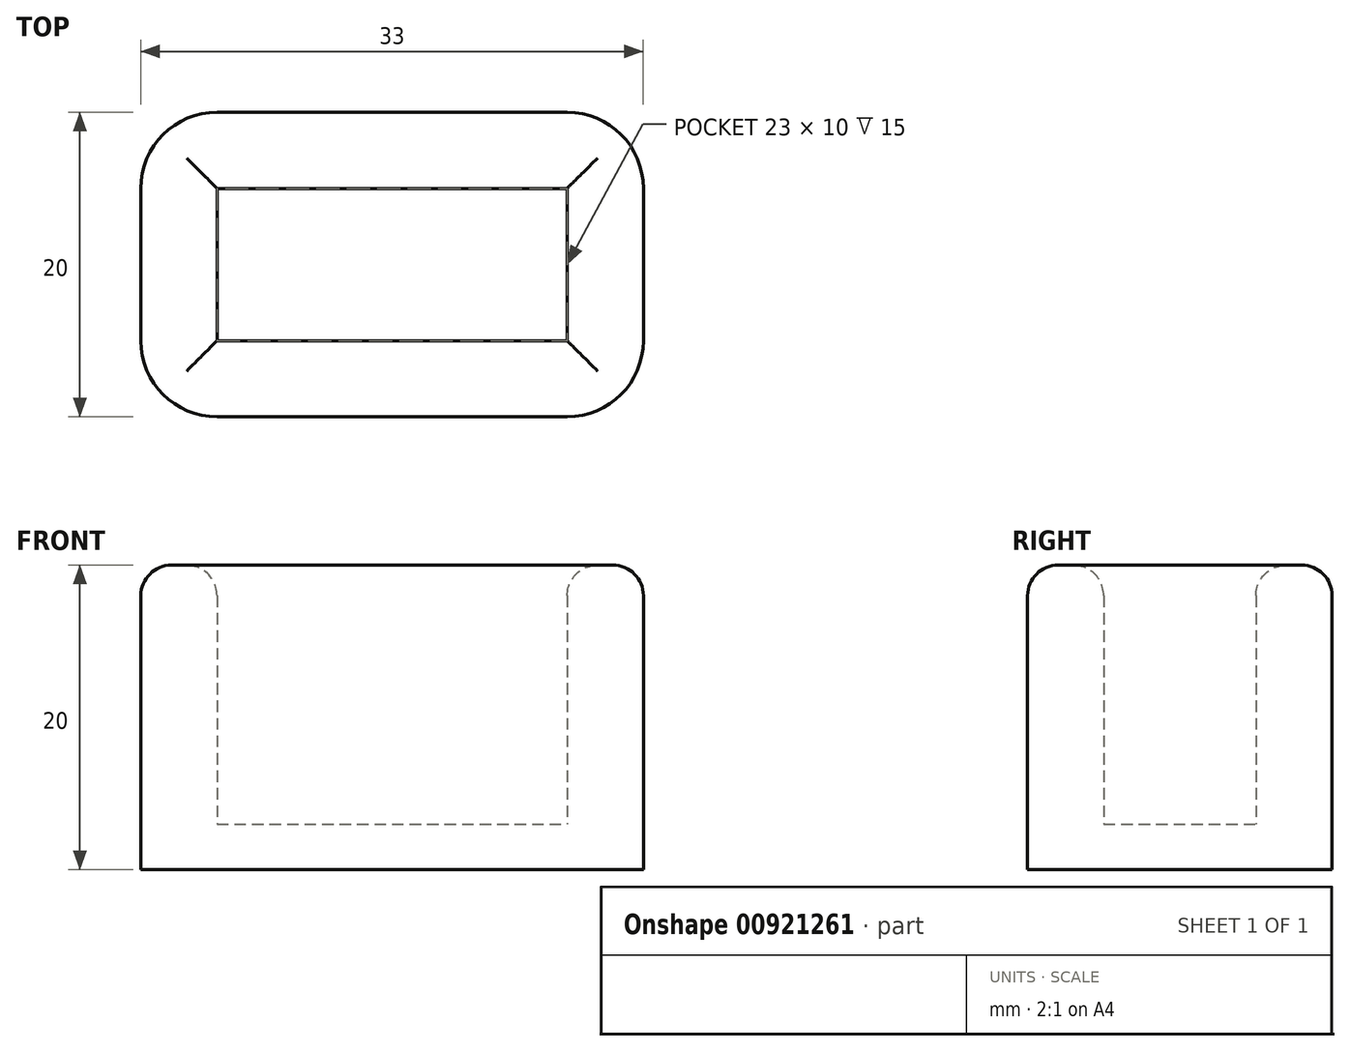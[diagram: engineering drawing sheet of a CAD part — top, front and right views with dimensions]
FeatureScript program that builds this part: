
annotation { "Feature Type Name" : "Feature", "Feature Type Description" : "" }
export const myFeature = defineFeature(function(context is Context, id is Id, definition is map)
    precondition{}
    {
        {
            var Q0;
            Q0=qCreatedBy(makeId("Top.planeOp"),FACE);
            var sketch = newSketch(context, id + "F0", { "sketchPlane" : qUnion([Q0])});
            skLineSegment(sketch, "E0.bottom", {"start": v(-38.39, 0) * mm, "end": v(-15.39, 0) * mm});
            skLineSegment(sketch, "E0.top", {"start": v(-38.39, 10) * mm, "end": v(-15.39, 10) * mm});
            skLineSegment(sketch, "E0.left", {"start": v(-38.39, 0) * mm, "end": v(-38.39, 10) * mm});
            skLineSegment(sketch, "E0.right", {"start": v(-15.39, 0) * mm, "end": v(-15.39, 10) * mm});
            skLineSegment(sketch, "E1.bottom", {"start": v(-38.39, 10) * mm, "end": v(-38.39, 10) * mm});
            skLineSegment(sketch, "E1.top", {"start": v(-38.39, 0) * mm, "end": v(-38.39, 0) * mm});
            skLineSegment(sketch, "E1.left", {"start": v(-38.39, 10) * mm, "end": v(-38.39, 0) * mm});
            skLineSegment(sketch, "E1.right", {"start": v(-38.39, 10) * mm, "end": v(-38.39, 0) * mm});
            skLineSegment(sketch, "E2.bottom", {"start": v(-15.39, 0) * mm, "end": v(-10.39, 0) * mm, "construction": true});
            skLineSegment(sketch, "E2.top", {"start": v(-15.39, 10) * mm, "end": v(-10.39, 10) * mm, "construction": true});
            skLineSegment(sketch, "E2.left", {"start": v(-15.39, 0) * mm, "end": v(-15.39, 10) * mm, "construction": true});
            skLineSegment(sketch, "E2.right", {"start": v(-10.39, 0) * mm, "end": v(-10.39, 10) * mm, "construction": true});
            skLineSegment(sketch, "E3.bottom", {"start": v(-38.39, 0) * mm, "end": v(-43.39, 0) * mm, "construction": true});
            skLineSegment(sketch, "E3.top", {"start": v(-38.39, 10) * mm, "end": v(-43.39, 10) * mm, "construction": true});
            skLineSegment(sketch, "E3.left", {"start": v(-38.39, 0) * mm, "end": v(-38.39, 10) * mm, "construction": true});
            skLineSegment(sketch, "E3.right", {"start": v(-43.39, 0) * mm, "end": v(-43.39, 10) * mm, "construction": true});
            skLineSegment(sketch, "E4.bottom", {"start": v(-38.39, 10) * mm, "end": v(-15.39, 10) * mm, "construction": true});
            skLineSegment(sketch, "E4.top", {"start": v(-38.39, 15) * mm, "end": v(-15.39, 15) * mm, "construction": true});
            skLineSegment(sketch, "E4.left", {"start": v(-38.39, 10) * mm, "end": v(-38.39, 15) * mm, "construction": true});
            skLineSegment(sketch, "E4.right", {"start": v(-15.39, 10) * mm, "end": v(-15.39, 15) * mm, "construction": true});
            skLineSegment(sketch, "E5.bottom", {"start": v(-15.39, 0) * mm, "end": v(-38.39, 0) * mm, "construction": true});
            skLineSegment(sketch, "E5.top", {"start": v(-15.39, -5) * mm, "end": v(-38.39, -5) * mm, "construction": true});
            skLineSegment(sketch, "E5.left", {"start": v(-15.39, 0) * mm, "end": v(-15.39, -5) * mm, "construction": true});
            skLineSegment(sketch, "E5.right", {"start": v(-38.39, 0) * mm, "end": v(-38.39, -5) * mm, "construction": true});
            skLineSegment(sketch, "E6.top", {"start": v(-38.39, 15) * mm, "end": v(-43.39, 15) * mm, "construction": true});
            skLineSegment(sketch, "E6.right", {"start": v(-43.39, 10) * mm, "end": v(-43.39, 15) * mm, "construction": true});
            skLineSegment(sketch, "E7.top", {"start": v(-38.39, -5) * mm, "end": v(-43.39, -5) * mm, "construction": true});
            skLineSegment(sketch, "E7.right", {"start": v(-43.39, 0) * mm, "end": v(-43.39, -5) * mm, "construction": true});
            skLineSegment(sketch, "E8.top", {"start": v(-15.39, -5) * mm, "end": v(-10.39, -5) * mm, "construction": true});
            skLineSegment(sketch, "E8.right", {"start": v(-10.39, 0) * mm, "end": v(-10.39, -5) * mm, "construction": true});
            skLineSegment(sketch, "E9.top", {"start": v(-15.39, 15) * mm, "end": v(-10.39, 15) * mm, "construction": true});
            skLineSegment(sketch, "E9.right", {"start": v(-10.39, 10) * mm, "end": v(-10.39, 15) * mm, "construction": true});
            skLineSegment(sketch, "E10.bottom", {"start": v(-43.39, 15) * mm, "end": v(-10.39, 15) * mm});
            skLineSegment(sketch, "E10.top", {"start": v(-43.39, -5) * mm, "end": v(-10.39, -5) * mm});
            skLineSegment(sketch, "E10.left", {"start": v(-43.39, 15) * mm, "end": v(-43.39, -5) * mm});
            skLineSegment(sketch, "E10.right", {"start": v(-10.39, 15) * mm, "end": v(-10.39, -5) * mm});
            skSolve(sketch);
        }
        {
            var Q0;
            Q0=makeQuery(id+"F0.imprint","IMPRINT",FACE,{"disambiguationData":[TD([[makeQuery(id+"F0.imprint","IMPRINT",EDGE,{"derivedFrom":sQuery(id+"F0.wireOp",EDGE,"E0.bottom")}),-1.0]])]});
            extrude(context, id + "F1", {"entities" : qUnion([Q0]), "depth" : 20 * mm, "offsetDistance" : 25 * mm});
        }
        {
            var Q0;
            Q0=makeQuery(id+"F0.imprint","IMPRINT",FACE,{"disambiguationData":[TD([[makeQuery(id+"F0.imprint","IMPRINT",EDGE,{"derivedFrom":sQuery(id+"F0.wireOp",EDGE,"E0.bottom")}),1.0]])]});
            extrude(context, id + "F2", {"entities" : qUnion([Q0]), "operationType" : NewBodyOperationType.ADD, "depth" : 3 * mm, "offsetDistance" : 25 * mm});
        }
        {
            var Q0;
            Q0=makeQuery(id+"F1.opExtrude","CAP_FACE",FACE,{"disambiguationData":[OSD([sQuery(id+"F0.wireOp",EDGE,"E0.bottom"),sQuery(id+"F0.wireOp",EDGE,"E0.top"),sQuery(id+"F0.wireOp",EDGE,"E0.right"),sQuery(id+"F0.wireOp",EDGE,"E1.right"),sQuery(id+"F0.wireOp",EDGE,"E10.bottom"),sQuery(id+"F0.wireOp",EDGE,"E10.top"),sQuery(id+"F0.wireOp",EDGE,"E10.left"),sQuery(id+"F0.wireOp",EDGE,"E10.right")])],"isStart":false});
            fillet(context, id + "F3", {"entities" : qUnion([Q0]), "radius" : 2 * mm, "tangentPropagation" : true, "allowEdgeOverflow" : false});
        }
        {
            var Q0;
            Q0=makeQuery(id+"F1.opExtrude","SWEPT_EDGE",EDGE,{"disambiguationData":[OSD([sQuery(id+"F0.wireOp",EDGE,"E10.bottom"),sQuery(id+"F0.wireOp",EDGE,"E10.left")])]});
            fillet(context, id + "F4", {"entities" : qUnion([Q0]), "radius" : 5 * mm, "tangentPropagation" : true, "allowEdgeOverflow" : false});
        }
        {
            var Q0;
            Q0=makeQuery(id+"F1.opExtrude","SWEPT_EDGE",EDGE,{"disambiguationData":[OSD([sQuery(id+"F0.wireOp",EDGE,"E10.bottom"),sQuery(id+"F0.wireOp",EDGE,"E10.right")])]});
            fillet(context, id + "F5", {"entities" : qUnion([Q0]), "radius" : 5 * mm, "tangentPropagation" : true, "allowEdgeOverflow" : false});
        }
        {
            var Q0;
            Q0=makeQuery(id+"F1.opExtrude","SWEPT_EDGE",EDGE,{"disambiguationData":[OSD([sQuery(id+"F0.wireOp",EDGE,"E10.top"),sQuery(id+"F0.wireOp",EDGE,"E10.right")])]});
            fillet(context, id + "F6", {"entities" : qUnion([Q0]), "radius" : 5 * mm, "tangentPropagation" : true, "allowEdgeOverflow" : false});
        }
        {
            var Q0;
            Q0=makeQuery(id+"F1.opExtrude","SWEPT_EDGE",EDGE,{"disambiguationData":[OSD([sQuery(id+"F0.wireOp",EDGE,"E10.top"),sQuery(id+"F0.wireOp",EDGE,"E10.left")])]});
            fillet(context, id + "F7", {"entities" : qUnion([Q0]), "radius" : 5 * mm, "tangentPropagation" : true, "allowEdgeOverflow" : false});
        }
    });
